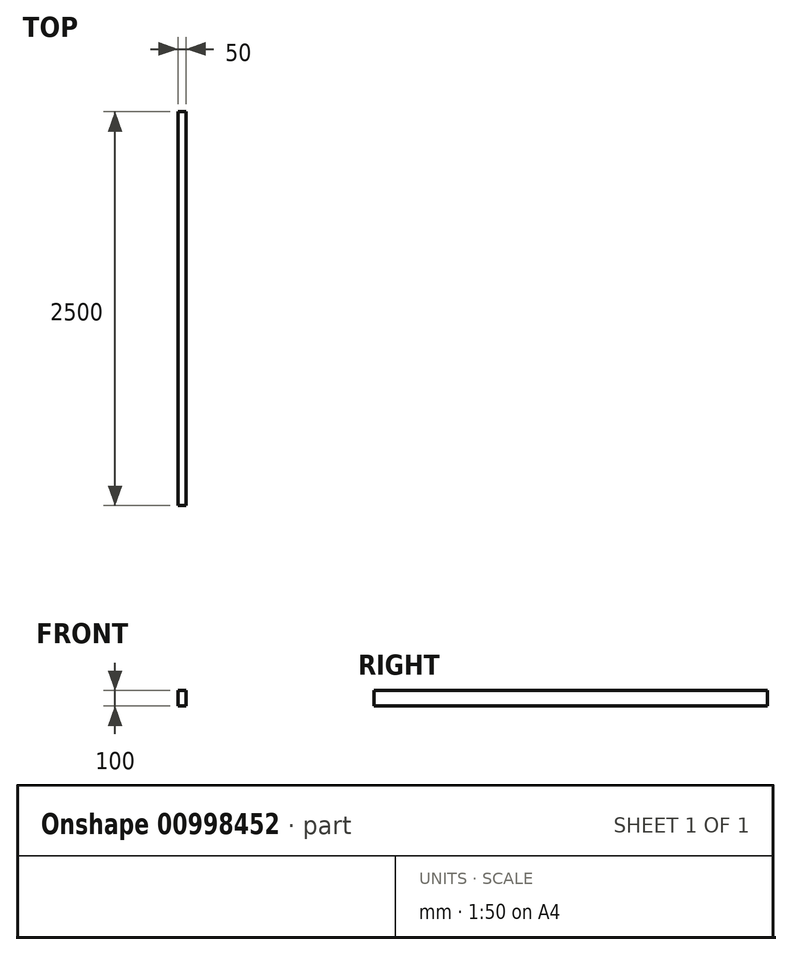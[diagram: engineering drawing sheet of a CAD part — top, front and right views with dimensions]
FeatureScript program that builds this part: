
annotation { "Feature Type Name" : "Feature", "Feature Type Description" : "" }
export const myFeature = defineFeature(function(context is Context, id is Id, definition is map)
    precondition{}
    {
        {
            var Q0;
            Q0=qCreatedBy(makeId("Front.planeOp"),FACE);
            var sketch = newSketch(context, id + "F0", { "sketchPlane" : qUnion([Q0])});
            skLineSegment(sketch, "E0.bottom", {"start": v(0, 0) * mm, "end": v(50, 0) * mm});
            skLineSegment(sketch, "E0.top", {"start": v(0, 100) * mm, "end": v(50, 100) * mm});
            skLineSegment(sketch, "E0.left", {"start": v(0, 0) * mm, "end": v(0, 100) * mm});
            skLineSegment(sketch, "E0.right", {"start": v(50, 0) * mm, "end": v(50, 100) * mm});
            skSolve(sketch);
        }
        {
            var Q0;
            Q0=makeQuery(id+"F0.imprint","IMPRINT",FACE,{"disambiguationData":[TD([[makeQuery(id+"F0.imprint","IMPRINT",EDGE,{"derivedFrom":sQuery(id+"F0.wireOp",EDGE,"E0.bottom")}),1.0]])]});
            extrude(context, id + "F1", {"entities" : qUnion([Q0]), "oppositeDirection" : true, "depth" : 2500 * mm, "offsetDistance" : 25.4 * mm});
        }
    });
